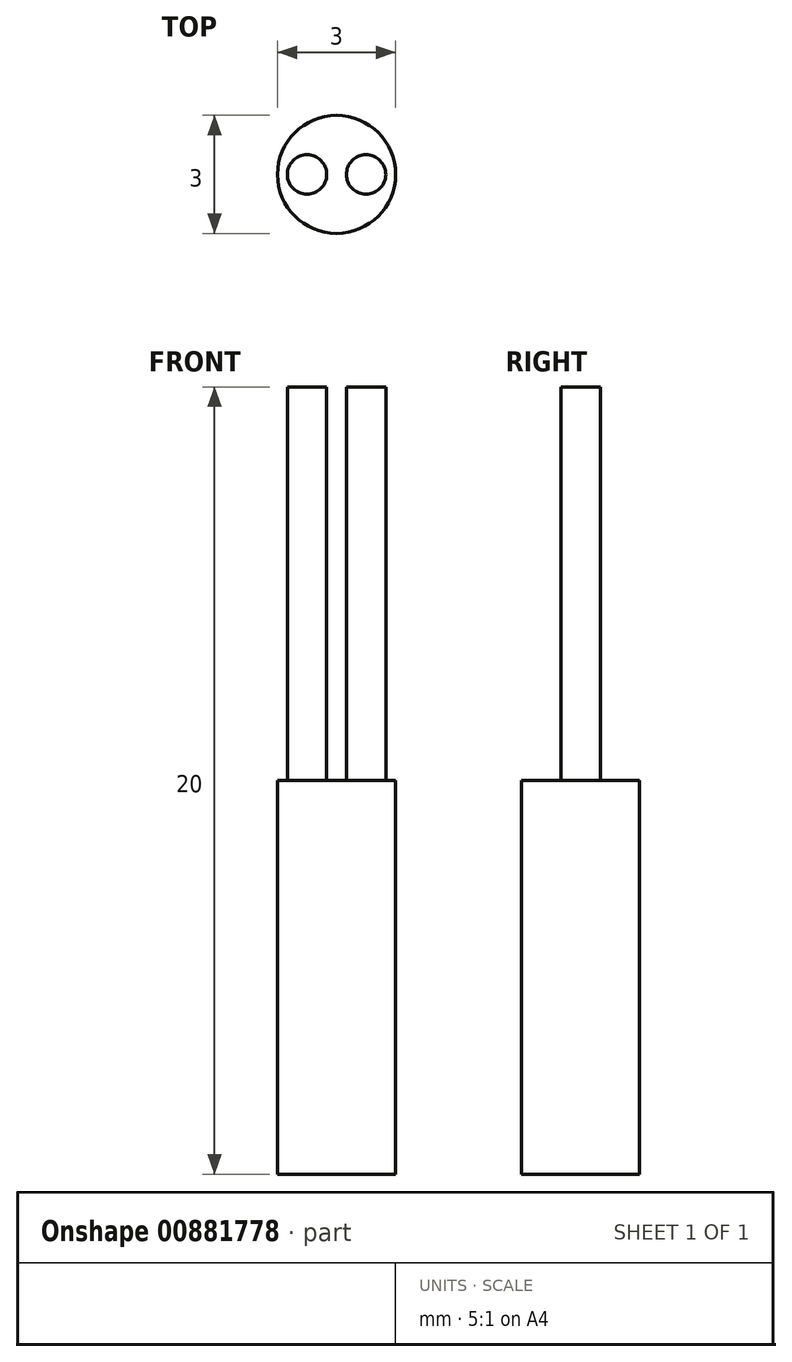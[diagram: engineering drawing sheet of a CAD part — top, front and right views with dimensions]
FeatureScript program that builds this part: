
annotation { "Feature Type Name" : "Feature", "Feature Type Description" : "" }
export const myFeature = defineFeature(function(context is Context, id is Id, definition is map)
    precondition{}
    {
        {
            var Q0;
            Q0=qCreatedBy(makeId("Top.planeOp"),FACE);
            var sketch = newSketch(context, id + "F0", { "sketchPlane" : qUnion([Q0])});
            skCircle(sketch, "E0", {"center": v(0, 0) * mm, "radius": 1.5 * mm});
            skSolve(sketch);
        }
        {
            var Q0;
            Q0 = qSketchRegion(id + "F0", true);
            extrude(context, id + "F1", {"entities" : qUnion([Q0]), "depth" : 10 * mm, "offsetDistance" : 25 * mm});
        }
        {
            var Q0;
            Q0=makeQuery(id+"F1.opExtrude","CAP_FACE",FACE,{"disambiguationData":[OSD([sQuery(id+"F0.wireOp",EDGE,"E0")])],"isStart":false});
            var sketch = newSketch(context, id + "F2", { "sketchPlane" : qUnion([Q0])});
            skCircle(sketch, "E1", {"center": v(-0.75, 0) * mm, "radius": 0.5 * mm});
            skCircle(sketch, "E2", {"center": v(0.75, 0) * mm, "radius": 0.5 * mm});
            skLineSegment(sketch, "E3", {"start": v(0, 1.75) * mm, "end": v(0, -1.7) * mm, "construction": true});
            skLineSegment(sketch, "E4", {"start": v(-1.75, 0) * mm, "end": v(1.81, 0) * mm, "construction": true});
            skSolve(sketch);
        }
        {
            var Q0;
            Q0 = qSketchRegion(id + "F2", true);
            extrude(context, id + "F3", {"entities" : qUnion([Q0]), "operationType" : NewBodyOperationType.ADD, "depth" : 10 * mm, "offsetDistance" : 25 * mm});
        }
    });
